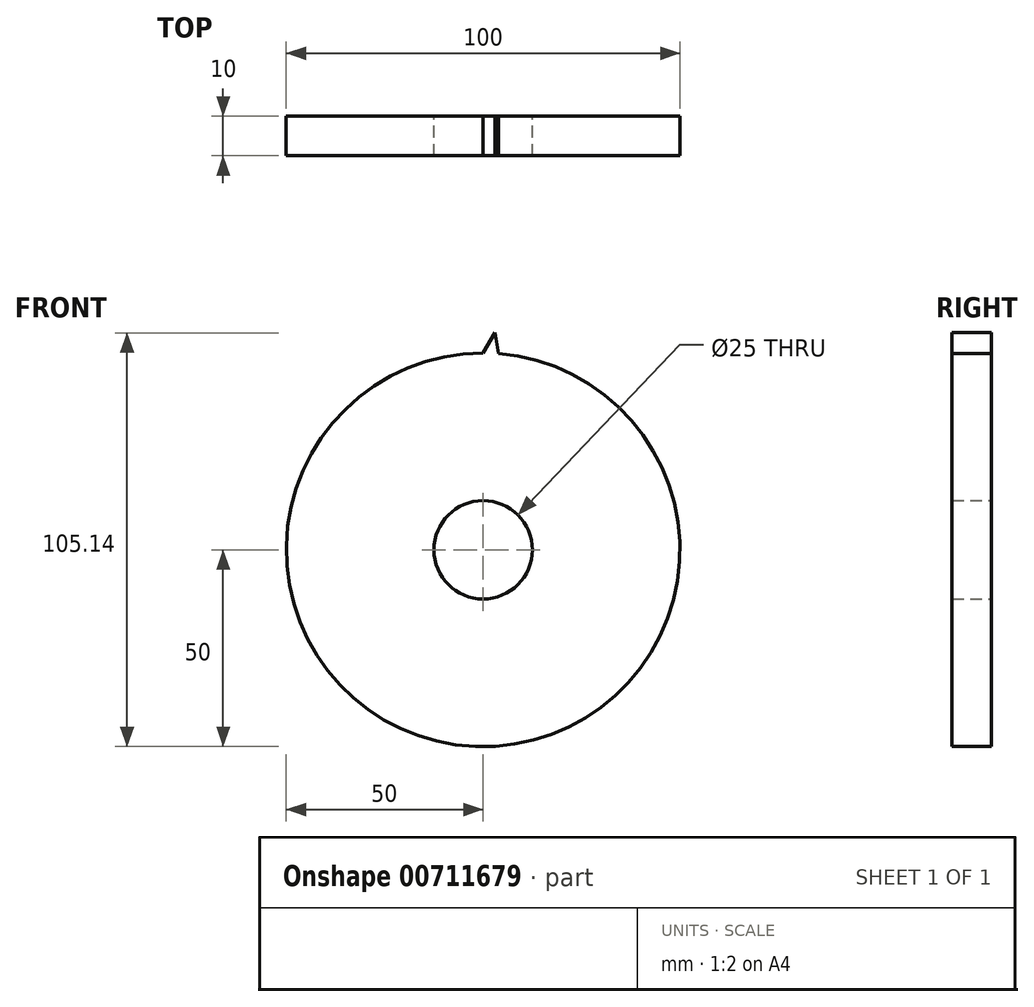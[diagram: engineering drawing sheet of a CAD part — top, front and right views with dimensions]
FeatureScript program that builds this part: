
annotation { "Feature Type Name" : "Feature", "Feature Type Description" : "" }
export const myFeature = defineFeature(function(context is Context, id is Id, definition is map)
    precondition{}
    {
        {
            var Q0;
            Q0=qCreatedBy(makeId("Front.planeOp"),FACE);
            var sketch = newSketch(context, id + "F0", { "sketchPlane" : qUnion([Q0])});
            skCircle(sketch, "E0", {"center": v(0, 0) * mm, "radius": 50 * mm});
            skCircle(sketch, "E1", {"center": v(0, 0) * mm, "radius": 12.5 * mm});
            skLineSegment(sketch, "E2", {"start": v(0, 0) * mm, "end": v(0, 50) * mm});
            skLineSegment(sketch, "E3", {"start": v(0, 50) * mm, "end": v(2.97, 55.14) * mm});
            skLineSegment(sketch, "E4", {"start": v(2.97, 55.14) * mm, "end": v(3.9, 49.85) * mm});
            skSolve(sketch);
        }
        {
            var Q0;
            Q0=makeQuery(id+"F0.imprint","IMPRINT",FACE,{"disambiguationData":[TD([[makeQuery(id+"F0.imprint","IMPRINT",EDGE,{"derivedFrom":sQuery(id+"F0.wireOp",EDGE,"E1")}),-1.0]])]});
            extrude(context, id + "F1", {"entities" : qUnion([Q0]), "depth" : 10 * mm, "offsetDistance" : 25 * mm});
        }
        {
            var Q0;
            {var subQ0=sQuery(id+"F0.wireOp",EDGE,"E3");Q0=makeQuery(id+"F0.imprint","IMPRINT",FACE,{"disambiguationData":[TD([[makeQuery(id+"F0.imprint","IMPRINT",EDGE,{"derivedFrom":subQ0}),-1.0]])]});}
            extrude(context, id + "F2", {"entities" : qUnion([Q0]), "operationType" : NewBodyOperationType.ADD, "depth" : 10 * mm, "offsetDistance" : 25 * mm});
        }
    });
